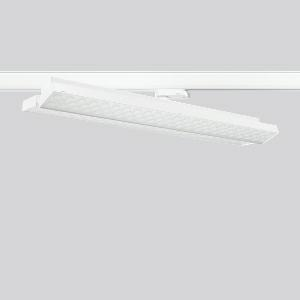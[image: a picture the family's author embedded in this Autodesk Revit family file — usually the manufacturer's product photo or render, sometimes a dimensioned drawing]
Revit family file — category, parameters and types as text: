
# Revit family: tx-move_742161_002_1_6582
name_source: partatom
category: Lighting Fixtures
units: mm (PartAtom-declared; Revit-internal decimal feet)

## family parameters
Cut with Voids When Loaded = No
Host = Face
Light Source = No
Part Type = Normal
Room Calculation Point = No
Round Connector Dimension = Use Diameter
Shared = No

## types (1)
- MultiLumen 1 (1 x LED Modul 840, 3125 lm, 4000)
    Apparent Load = 41 VA
    CIE Flux Codes = 90 97 99 100 100
    Color Rendering = 80
    Color Temperature = 4000
    Default Elevation = 1800 mm
    Description = Series: TX-MOVE
Multifunctional surface-mounted spotlight for area lighting. Very flat design. Housing: sheet steel, powder-coated. Rotation range: 356°. Swivel range: 90°. Consistent alignment possible with visible tilt scale. High-efficiency LED units with optimum light control thanks to clear plastic (PC) lens optics. Spezielle Mikrostrukturen reduzieren Gelbsaum. Symmetrical light distribution. With multi adaptor for 3-circuit tracks 230 V. Suitable for Track on ceiling. MultiLumen: Luminous flux adjustable in 3 steps. Factory setting is the highest luminous flux. Environmentally friendly and resource-saving due to replaceable and recyclable components. Very good glare control, ideal for till areas. 
Colour: traffic white, matt (RAL 9016)
Length: 570 mm
Width: 119 mm
Height: 92 mm
Lamp: LED
Socket: without socket
Colour temperature: 4000K
Colour rendering index (CRI): 80
System power: 41 W
Rated luminous flux: 6250 lm
Luminous efficiency: 152 lm/W
System power 2: 57 W
Rated luminous flux 2: 8450 lm
Luminous efficiency 2: 148 lm/W
System power 3: 73 W
Rated luminous flux 3: 10400 lm
Luminous efficiency 3: 142 lm/W
Control gear: Regulated power supply
Protection class: I
Type of protection: IP 20
    Height = 75 mm
    Lamp = 1 x LED Modul 840
    Lamp Light Flux = 3125 lm
    Lamp count = 1
    Length = 569 mm
    Lifetime = 50000 h
    Luminous efficacy = 152 lm/W
    Manufacturer = RZB
    ModVariant = No
    Model = 742161.002.1
    Mounting Place = Ceiling
    Mounting Type = Surface mounted
    Number of Poles = 1
    OnlyDefault = Yes
    Power Factor = 1
    Product Name = TX-MOVE
    Product group = Track mounted projectors
    ProductGroupID = 301
    Protection Class = Protection class I
    Protection Degree = IP 20
    RLX_Detail_Level = 1
    RLX_Emergency_Light_Flux = 0 lm
    RLX_Emergency_Type = 0
    RLX_Emergency_Type_DB = No
    RlxData = <blob elided: 31233 chars, md5=bc66ef5f>
    Socket = socket
    Standby Power = 0 W
    System Light Flux = 6250 lm
    System Power = 41 W
    Type Comments = MultiLumen 1
    Type Image = 742162.002.jpg
    URL = http://relux.com
    VarID = multilumen_1
    Voltage = 0 V
    Weight = 0.00 kg
    Width = 119 mm

## geometry (parser evidence)
native form markers: Blend x4, Sweep x15
no freeform markers — native parametric forms only
